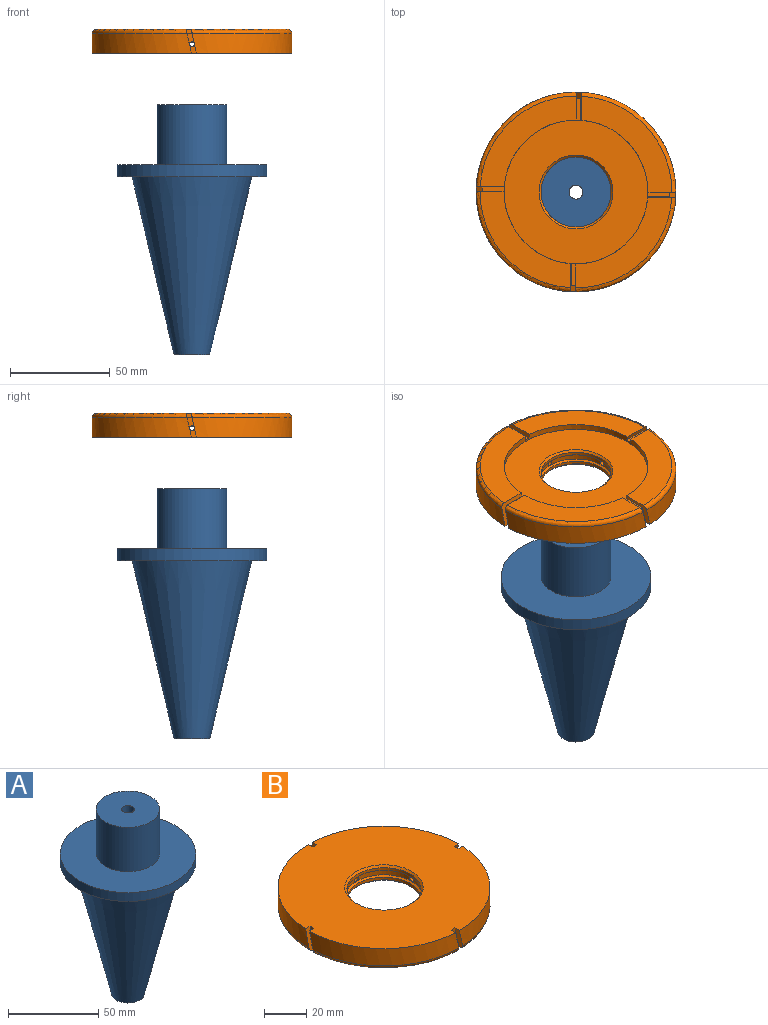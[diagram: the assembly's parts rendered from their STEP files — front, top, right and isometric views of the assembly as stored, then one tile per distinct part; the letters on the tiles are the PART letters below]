
ASSEMBLY  parts=2 mates=1
PART A: 10 faces, bbox 75x75x125 mm
  f0: cylinder r=3.5mm len=105mm, axis (0,0,-1), area 2309.1mm2, adj f1,f9
  f1: plane 35x35mm, normal (0,0,1), area 923.6mm2, adj f0,f2
  f2: cylinder r=17.5mm len=35mm, axis (0,0,-1), area 3298.7mm2, adj f1,f3
  f3: plane 75x75mm, normal (0,0,1), area 3455.8mm2, adj f2,f4
  f4: cylinder r=37.5mm len=75mm, axis (0,0,-1), area 1413.7mm2, adj f3,f5
  f5: plane 75x75mm, normal (0,0,-1), area 1590.4mm2, adj f4,f6
  f6: cone r=9mm half-angle=13.3deg, axis (0,0,1), area 11203.9mm2, adj f5,f7
  f7: plane 18x18mm, normal (0,0,-1), area 100.5mm2, adj f6,f8
  f8: cylinder r=7mm len=20mm, axis (0,0,-1), area 879.6mm2, adj f7,f9
  f9: plane 14x14mm, normal (0,0,-1), area 115.5mm2, adj f0,f8
PART B: 50 faces, bbox 108.2x108.2x12 mm
  f0: cylinder r=17.5mm len=35mm, axis (0,0,-1), area 164.9mm2, adj f23,f48
  f1: plane 48.29x45.06mm, normal (0,0,-1), area 760.9mm2, adj f4,f19,f25,f39
  f2: plane 100x100mm, normal (0,0,1), area 6748.2mm2, adj f3,f7,f12,f16,f23,f24,f25,f26
  f3: cylinder r=50mm len=49.94mm, axis (0,0,-1), area 759.8mm2, adj f2,f4,f25,f39
  f4: torus R=48mm, axis (0,0,1), area 235.1mm2, adj f1,f3,f25,f39
  f5: cylinder r=1.25mm len=28.54mm, axis (1,0,0), area 224mm2, adj f41,f42,f44,f45
  f6: plane 48.29x45.06mm, normal (0,0,-1), area 760.9mm2, adj f8,f19,f20,f34,f40
  f7: cylinder r=50mm len=49.94mm, axis (0,0,-1), area 759.8mm2, adj f2,f8,f34,f40
  f8: torus R=48mm, axis (0,0,1), area 235.1mm2, adj f6,f7,f34,f40
  f9: cylinder r=1.25mm len=28.54mm, axis (0,-1,0), area 224mm2, adj f36,f37,f44,f46
  f10: plane 48.29x45.06mm, normal (0,0,-1), area 760.9mm2, adj f13,f19,f31,f35
  f11: cylinder r=1.25mm len=28.54mm, axis (1,0,0), area 224mm2, adj f29,f30,f46,f47
  f12: cylinder r=50mm len=49.94mm, axis (0,0,-1), area 759.8mm2, adj f2,f13,f31,f35
  f13: torus R=48mm, axis (0,0,1), area 235.1mm2, adj f10,f12,f31,f35
  f14: cylinder r=1.25mm len=28.54mm, axis (0,-1,0), area 224mm2, adj f26,f27,f45,f47
  f15: cylinder r=17.5mm len=35mm, axis (0,0,-1), area 164.9mm2, adj f22,f49
  f16: cylinder r=50mm len=49.94mm, axis (0,0,-1), area 759.8mm2, adj f2,f18,f24,f32
  f17: plane 48.29x45.06mm, normal (0,0,-1), area 760.9mm2, adj f18,f19,f24,f32
  f18: torus R=48mm, axis (0,0,1), area 235.1mm2, adj f16,f17,f24,f32
  f19: cylinder r=36mm len=72mm, axis (0,0,-1), area 657.7mm2, adj f1,f6,f10,f17,f20,f21,f24,f25
  f20: cylinder r=36mm len=1.72mm, axis (0,0,-1), area 0.3mm2, adj f6,f19,f40
  f21: plane 72x72mm, normal (0,0,-1), area 2996.3mm2, adj f19,f22
  f22: cone r=18.5mm half-angle=45deg, axis (0,0,-1), area 159.9mm2, adj f15,f21
  f23: cone r=17.5mm half-angle=45deg, axis (0,0,1), area 159.9mm2, adj f0,f2
  f24: plane 14.12x12mm, normal (-0.98,0,-0.22), area 58.3mm2, adj f2,f16,f17,f18,f19,f26,f27,f28
  f25: plane 14x12mm, normal (0.98,0,0.22), area 58.3mm2, adj f1,f2,f3,f4,f19,f26,f27,f28
  f26: plane 4.77x3.5mm, normal (0,-1,0), area 9.1mm2, adj f2,f14,f24,f25
  f27: plane 5.77x3.72mm, normal (0,-1,0), area 11.6mm2, adj f14,f24,f25,f28
  f28: plane 11.09x2.56mm, normal (0,0,-1), area 28.2mm2, adj f19,f24,f25,f27
  f29: plane 4.77x3.5mm, normal (1,0,0), area 9.1mm2, adj f2,f11,f31,f32
  f30: plane 5.77x3.72mm, normal (1,0,0), area 11.6mm2, adj f11,f31,f32,f33
  f31: plane 14.12x12mm, normal (0,-0.98,-0.22), area 58.3mm2, adj f2,f10,f12,f13,f19,f29,f30,f33
  f32: plane 14x12mm, normal (0,0.98,0.22), area 58.3mm2, adj f2,f16,f17,f18,f19,f29,f30,f33
  f33: plane 11.09x2.56mm, normal (0,0,-1), area 28.2mm2, adj f19,f30,f31,f32
  f34: plane 14.12x12mm, normal (0.98,0,-0.22), area 58.3mm2, adj f2,f6,f7,f8,f19,f36,f37,f38
  f35: plane 14x12mm, normal (-0.98,0,0.22), area 58.3mm2, adj f2,f10,f12,f13,f19,f36,f37,f38
  f36: plane 4.77x3.5mm, normal (0,1,0), area 9.1mm2, adj f2,f9,f34,f35
  f37: plane 5.77x3.72mm, normal (0,1,0), area 11.6mm2, adj f9,f34,f35,f38
  f38: plane 11.09x2.56mm, normal (0,0,-1), area 28.2mm2, adj f19,f34,f35,f37
  f39: plane 14.12x12mm, normal (0,0.98,-0.22), area 58.3mm2, adj f1,f2,f3,f4,f19,f41,f42,f43
  f40: plane 14x12mm, normal (0,-0.98,0.22), area 58.3mm2, adj f2,f6,f7,f8,f19,f20,f41,f42
  f41: plane 4.77x3.5mm, normal (-1,0,0), area 9.1mm2, adj f2,f5,f39,f40
  f42: plane 5.77x3.72mm, normal (-1,0,0), area 11.6mm2, adj f5,f39,f40,f43
  f43: plane 11.09x2.56mm, normal (0,0,-1), area 28.2mm2, adj f19,f39,f40,f42
  f44: cylinder r=18.5mm len=18.5mm, axis (0,0,1), area 67.7mm2, adj f5,f9,f48,f49
  f45: cylinder r=18.5mm len=18.5mm, axis (0,0,1), area 67.7mm2, adj f5,f14,f48,f49
  f46: cylinder r=18.5mm len=18.5mm, axis (0,0,1), area 67.7mm2, adj f9,f11,f48,f49
  f47: cylinder r=18.5mm len=18.5mm, axis (0,0,1), area 67.7mm2, adj f11,f14,f48,f49
  f48: cone r=17.5mm half-angle=53.1deg, axis (0,0,-1), area 141.4mm2, adj f0,f44,f45,f46,f47
  f49: cone r=18.5mm half-angle=53.1deg, axis (0,0,1), area 141.4mm2, adj f15,f44,f45,f46,f47
PLACE A t=(-42.6,44.98,-10.27)mm
PLACE B rot(axis=(0.71,-0.71,0),180deg) t=(-42.6,44.98,152.48)mm
MATE slider B.f0 <-> A.f0  axis (0,0,1) through (-42.6,44.98,142.23)mm
